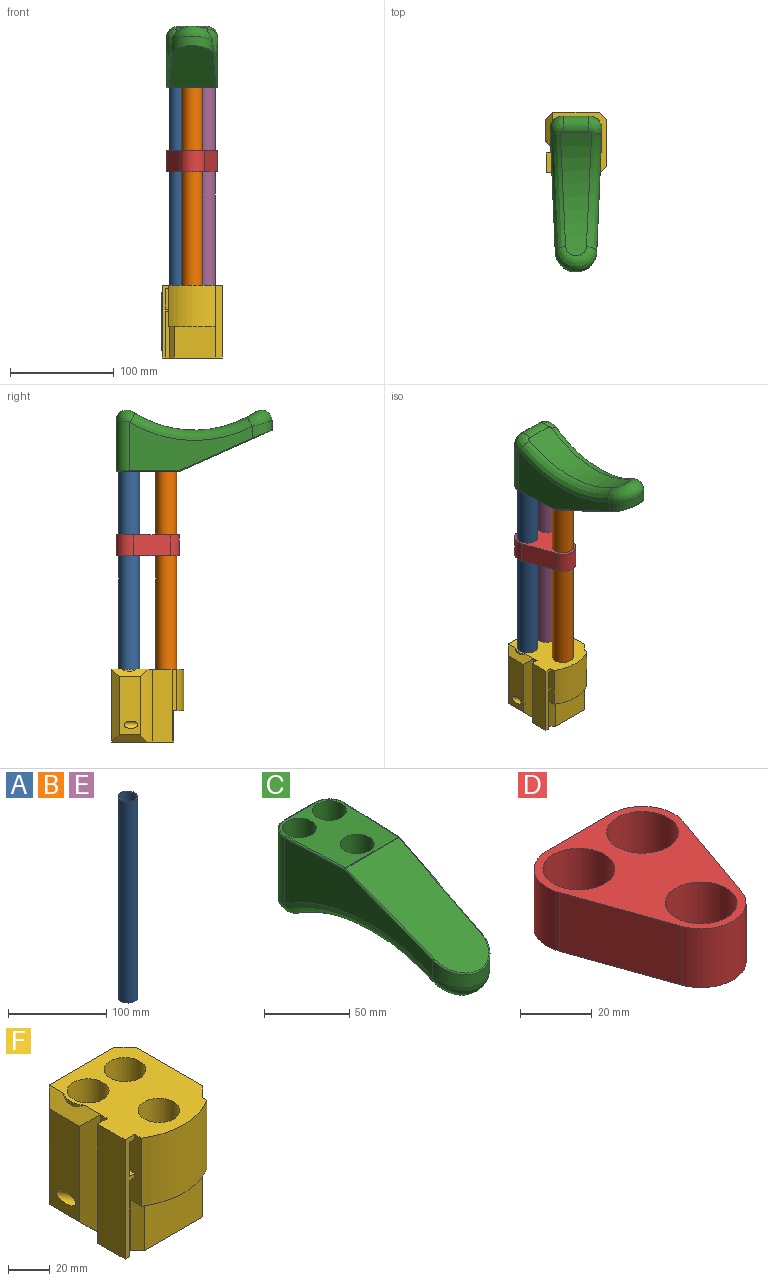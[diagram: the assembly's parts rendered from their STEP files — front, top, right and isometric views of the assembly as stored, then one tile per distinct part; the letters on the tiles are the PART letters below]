
ASSEMBLY  parts=6 mates=5
PART A: 4 faces, bbox 20x20x250 mm
  f0: cylinder r=8.5mm len=250mm, axis (0,0,-1), area 13351.8mm2, adj f2,f3
  f1: cylinder r=10mm len=250mm, axis (0,0,-1), area 15708mm2, adj f2,f3
  f2: plane 20x20mm, normal (0,0,1), area 87.2mm2, adj f0,f1
  f3: plane 20x20mm, normal (0,0,-1), area 87.2mm2, adj f0,f1
PART B: same geometry as A
PART C: 32 faces, bbox 53.2x151.1x67.9 mm
  f0: plane 88.71x43.96mm, normal (0,-0.41,0.91), area 3751.6mm2, adj f20,f21,f23,f25
  f1: cylinder r=108.75mm len=119.05mm, axis (-1,0,0), area 3062.2mm2, adj f9,f10,f11,f12,f13,f14
  f2: plane 48.37x25mm, normal (0,1,0), area 1209.2mm2, adj f7,f8,f11,f17
  f3: plane 59.29x48mm, normal (0,0,1), area 1750.5mm2, adj f15,f16,f17,f19,f21,f22,f26,f28
  f4: plane 117.82x46.71mm, normal (1,-0.04,0), area 2912.2mm2, adj f6,f7,f14,f22,f25
  f5: plane 117.82x46.71mm, normal (-1,-0.04,0), area 2912.2mm2, adj f6,f8,f10,f16,f20
  f6: cylinder r=20mm len=39.96mm, axis (0,0,1), area 583.1mm2, adj f4,f5,f12,f23
  f7: cylinder r=12.5mm len=48.37mm, axis (0,0,1), area 963.1mm2, adj f2,f4,f13,f19
  f8: cylinder r=12.5mm len=48.37mm, axis (0,0,1), area 963.1mm2, adj f2,f5,f9,f15
  f9: bspline ~20.26x18.91mm, area 300.4mm2, adj f1,f8,f10,f11
  f10: bspline ~117.82x26.22mm, area 1833.9mm2, adj f1,f5,f9,f12
  f11: cylinder r=10mm len=25mm, axis (-1,0,0), area 537.5mm2, adj f1,f2,f9,f13
  f12: bspline ~41.52x26.02mm, area 1036.6mm2, adj f1,f6,f10,f14
  f13: bspline ~20.61x20.59mm, area 300.4mm2, adj f1,f7,f11,f14
  f14: bspline ~117.82x26.22mm, area 1833.9mm2, adj f1,f4,f12,f13
  f15: torus R=11.5mm, axis (0,0,1), area 30.8mm2, adj f3,f8,f16,f17
  f16: cylinder r=1mm len=47.34mm, axis (0.04,-1,0), area 74.4mm2, adj f3,f5,f15,f18
  f17: cylinder r=1mm len=25mm, axis (1,0,0), area 39.3mm2, adj f2,f3,f15,f19
  f18: sphere r=1mm, area 0.4mm2, adj f16,f20,f21
  f19: torus R=11.5mm, axis (0,0,1), area 30.8mm2, adj f3,f7,f17,f22
  f20: cylinder r=1mm len=70.89mm, axis (0.04,-0.91,-0.41), area 120.1mm2, adj f0,f5,f18,f23
  f21: cylinder r=1mm len=43.96mm, axis (1,0,0), area 18.5mm2, adj f0,f3,f18,f24
  f22: cylinder r=1mm len=47.34mm, axis (0.04,1,0), area 74.4mm2, adj f3,f4,f19,f24
  f23: bspline ~39.96x19.14mm, area 81.4mm2, adj f0,f6,f20,f25
  f24: sphere r=1mm, area 0.4mm2, adj f21,f22,f25
  f25: cylinder r=1mm len=70.89mm, axis (0.04,0.91,0.41), area 120.1mm2, adj f0,f4,f23,f24
  f26: cylinder r=10mm len=30mm, axis (0,0,1), area 1885mm2, adj f3,f27
  f27: plane 20x20mm, normal (0,0,1), area 314.2mm2, adj f26
  f28: cylinder r=10mm len=30mm, axis (0,0,1), area 1885mm2, adj f3,f29
  f29: plane 20x20mm, normal (0,0,1), area 314.2mm2, adj f28
  f30: cylinder r=10mm len=30mm, axis (0,0,1), area 1885mm2, adj f3,f31
  f31: plane 20x20mm, normal (0,0,1), area 314.2mm2, adj f30
PART D: 11 faces, bbox 50x60.5x20 mm
  f0: plane 25x20mm, normal (0,1,0), area 500mm2, adj f1,f8,f9,f10
  f1: cylinder r=12.5mm len=20mm, axis (0,0,-1), area 477.3mm2, adj f0,f2,f9,f10
  f2: plane 35.5x20mm, normal (-0.94,-0.33,0), area 752.7mm2, adj f1,f3,f9,f10
  f3: cylinder r=12.5mm len=23.58mm, axis (0,0,-1), area 616.1mm2, adj f2,f4,f9,f10
  f4: plane 35.5x20mm, normal (0.94,-0.33,0), area 752.7mm2, adj f3,f8,f9,f10
  f5: cylinder r=10mm len=20mm, axis (0,0,-1), area 1256.6mm2, adj f9,f10
  f6: cylinder r=10mm len=20mm, axis (0,0,-1), area 1256.6mm2, adj f9,f10
  f7: cylinder r=10mm len=20mm, axis (0,0,-1), area 1256.6mm2, adj f9,f10
  f8: cylinder r=12.5mm len=20mm, axis (0,0,-1), area 477.3mm2, adj f0,f4,f9,f10
  f9: plane 60.5x50mm, normal (0,0,1), area 1245.6mm2, adj f0,f1,f2,f3,f4,f5,f6,f7
  f10: plane 60.5x50mm, normal (0,0,-1), area 1245.6mm2, adj f0,f1,f2,f3,f4,f5,f6,f7
PART E: same geometry as A
PART F: 69 faces, bbox 72.7x71.4x72.4 mm
  f0: plane 20x3.1mm, normal (1,0,0), area 62mm2, adj f5,f56,f61,f64
  f1: plane 20x3.1mm, normal (1,0,0), area 62mm2, adj f4,f59,f62,f66
  f2: plane 40x7.71mm, normal (-1,0,0), area 291.3mm2, adj f4,f6,f8,f35,f37,f59,f62,f65
  f3: plane 70x7.71mm, normal (-1,0,0), area 522.5mm2, adj f5,f7,f8,f9,f53,f56,f61,f63
  f4: plane 20x3.5mm, normal (0,-1,0), area 70mm2, adj f1,f2,f62,f66
  f5: plane 20x3.5mm, normal (0,1,0), area 70mm2, adj f0,f3,f61,f64
  f6: plane 44.5x3.79mm, normal (0,-1,0), area 164.5mm2, adj f2,f9,f37,f57,f60,f65
  f7: plane 44.5x3.5mm, normal (0,1,0), area 155.7mm2, adj f3,f9,f55,f63
  f8: plane 69x57.9mm, normal (0,0,1), area 2542.2mm2, adj f2,f3,f11,f12,f13,f14,f35,f36
  f9: plane 59.5x57.9mm, normal (0,0,-1), area 1758.8mm2, adj f3,f6,f7,f10,f11,f12,f13,f14
  f10: plane 39.5x30mm, normal (0,-1,0), area 1185mm2, adj f9,f11,f37,f60
  f11: plane 70x7mm, normal (0.71,-0.71,0), area 693mm2, adj f8,f9,f10,f12,f36
  f12: plane 72.36x47.86mm, normal (1,0,0), area 3112.4mm2, adj f8,f9,f11,f13,f30
  f13: plane 70x7mm, normal (0.71,0.71,0), area 693mm2, adj f8,f9,f12,f14
  f14: plane 70x44.5mm, normal (0,1,0), area 3115mm2, adj f8,f9,f13,f15
  f15: plane 70x7mm, normal (-0.71,0.71,0), area 623.7mm2, adj f14,f24,f54,f67
  f16: plane 30x28.79mm, normal (0,1,0), area 813.6mm2, adj f9,f17,f23,f28,f33,f40
  f17: plane 30x7.77mm, normal (0.85,0.53,0), area 274.9mm2, adj f9,f16,f18,f39
  f18: plane 30x23.97mm, normal (1,-0.05,0), area 707.7mm2, adj f9,f17,f19,f25,f41
  f19: plane 30x5.76mm, normal (0.85,-0.53,0), area 203.8mm2, adj f9,f18,f20,f43
  f20: plane 30x28.79mm, normal (0,-1,0), area 863.6mm2, adj f9,f19,f21,f45
  f21: plane 30x5.76mm, normal (-0.85,-0.53,0), area 203.8mm2, adj f9,f20,f22,f46
  f22: plane 30x23.97mm, normal (-1,-0.05,0), area 707.7mm2, adj f9,f21,f23,f32,f44
  f23: plane 30x7.77mm, normal (-0.85,0.53,0), area 274.9mm2, adj f9,f16,f22,f42
  f24: plane 58.36x23.14mm, normal (-1,0,0), area 1091.3mm2, adj f15,f27,f53,f54,f67
  f25: cylinder r=1.5mm len=11.23mm, axis (-0.53,0.85,0), area 86.9mm2, adj f18,f26
  f26: plane 7x5.94mm, normal (-0.53,0.85,0), area 31.4mm2, adj f25,f27
  f27: cylinder r=3.5mm len=16.86mm, axis (-0.53,0.85,0), area 217.9mm2, adj f24,f26
  f28: cylinder r=1.5mm len=5.39mm, axis (-0.53,0.85,0), area 15.7mm2, adj f16,f29
  f29: plane 3x2.54mm, normal (-0.53,0.85,0), area 7.1mm2, adj f28
  f30: cylinder r=3.5mm len=16.86mm, axis (0.53,0.85,0), area 217.9mm2, adj f12,f31
  f31: plane 7x5.94mm, normal (0.53,0.85,0), area 31.4mm2, adj f30,f32
  f32: cylinder r=1.5mm len=11.23mm, axis (0.53,0.85,0), area 86.9mm2, adj f22,f31
  f33: cylinder r=1.5mm len=5.39mm, axis (0.53,0.85,0), area 15.7mm2, adj f16,f34
  f34: plane 3x2.54mm, normal (0.53,0.85,0), area 7.1mm2, adj f33
  f35: cylinder r=41.33mm len=44.5mm, axis (0,0,-1), area 1879.6mm2, adj f2,f8,f36,f37
  f36: plane 40x3mm, normal (1,0,0), area 120mm2, adj f8,f11,f35,f37
  f37: plane 44.5x14.21mm, normal (0,0,-1), area 342mm2, adj f2,f6,f10,f35,f36,f60
  f38: plane 28.35x27.5mm, normal (0,0,-1), area 737.4mm2, adj f39,f40,f41,f42,f43,f44,f45,f46
  f39: plane 9.08x7.63mm, normal (0.6,0.37,-0.71), area 49.4mm2, adj f17,f38,f40,f41
  f40: plane 28.79x5mm, normal (0,0.71,-0.71), area 184mm2, adj f16,f38,f39,f42
  f41: plane 23.97x6.18mm, normal (0.71,-0.04,-0.71), area 159.6mm2, adj f18,f38,f39,f43
  f42: plane 9.08x7.63mm, normal (-0.6,0.37,-0.71), area 49.4mm2, adj f23,f38,f40,f44
  f43: plane 7.31x6.37mm, normal (0.6,-0.37,-0.71), area 33.7mm2, adj f19,f38,f41,f45
  f44: plane 23.97x6.18mm, normal (-0.71,-0.04,-0.71), area 159.6mm2, adj f22,f38,f42,f46
  f45: plane 28.79x5mm, normal (0,-0.71,-0.71), area 184mm2, adj f20,f38,f43,f46
  f46: plane 7.31x6.37mm, normal (-0.6,-0.37,-0.71), area 33.7mm2, adj f21,f38,f44,f45
  f47: cylinder r=10mm len=30mm, axis (0,0,1), area 1885mm2, adj f8,f48
  f48: plane 20x20mm, normal (0,0,1), area 314.2mm2, adj f47
  f49: cylinder r=10mm len=30mm, axis (0,0,1), area 1885mm2, adj f8,f50
  f50: plane 20x20mm, normal (0,0,1), area 314.2mm2, adj f49
  f51: cylinder r=10mm len=30mm, axis (0,0,1), area 1885mm2, adj f8,f52
  f52: plane 20x20mm, normal (0,0,1), area 314.2mm2, adj f51
  f53: plane 70x7mm, normal (-0.71,-0.71,0), area 623.7mm2, adj f3,f24,f54,f67
  f54: plane 34.78x7mm, normal (-0.71,0,-0.71), area 275.1mm2, adj f9,f15,f24,f53
  f55: plane 44.5x3.1mm, normal (1,0,0), area 138mm2, adj f7,f9,f56,f63
  f56: plane 70x6.4mm, normal (0,1,0), area 222.2mm2, adj f0,f3,f8,f9,f55,f58,f61,f63
  f57: plane 44.5x3.1mm, normal (1,0,0), area 138mm2, adj f6,f9,f59,f65
  f58: plane 70x18.5mm, normal (-1,0,0), area 1295mm2, adj f8,f9,f56,f59
  f59: plane 70x6.4mm, normal (0,-1,0), area 222.2mm2, adj f1,f2,f8,f9,f57,f58,f62,f65
  f60: plane 30x4.71mm, normal (-0.71,-0.71,0), area 199.7mm2, adj f6,f9,f10,f37
  f61: plane 3.5x3.1mm, normal (0,0,-1), area 10.9mm2, adj f0,f3,f5,f56
  f62: plane 3.5x3.1mm, normal (0,0,-1), area 10.9mm2, adj f1,f2,f4,f59
  f63: plane 3.5x3.1mm, normal (0,0,-1), area 10.9mm2, adj f3,f7,f55,f56
  f64: plane 3.5x3.1mm, normal (0,0,1), area 10.9mm2, adj f0,f3,f5,f56
  f65: plane 3.5x3.1mm, normal (0,0,-1), area 10.9mm2, adj f2,f6,f57,f59
  f66: plane 3.5x3.1mm, normal (0,0,1), area 10.9mm2, adj f1,f2,f4,f59
  f67: plane 34.78x7mm, normal (-0.71,0,0.71), area 244.8mm2, adj f8,f15,f24,f53,f68
  f68: cylinder r=12mm len=13.99mm, axis (0,0,1), area 22.3mm2, adj f8,f67
PLACE A t=(-12.48,119.17,-152.74)mm
PLACE B t=(0.02,83.67,-152.74)mm
PLACE C rot(axis=(0,-1,0),180deg) t=(0.02,112.53,-57.74)mm
PLACE D t=(0.02,112.53,-128.43)mm
PLACE E t=(12.52,119.17,-152.74)mm
PLACE F t=(0.02,112.53,-317.74)mm
MATE slider E.f0 <-> D.f6  axis (0,0,-1) through (12.52,122.03,-152.74)mm
MATE fastened F.f49 <-> E.f0  axis (0,0,1) through (12.52,122.03,-277.74)mm
MATE fastened C.f30 <-> B.f0  axis (0,0,-1) through (0.02,86.53,-27.74)mm
MATE fastened B.f0 <-> F.f51  axis (0,0,-1) through (0.02,86.53,-277.74)mm
MATE fastened F.f47 <-> A.f0  axis (0,0,1) through (-12.48,122.03,-277.74)mm
